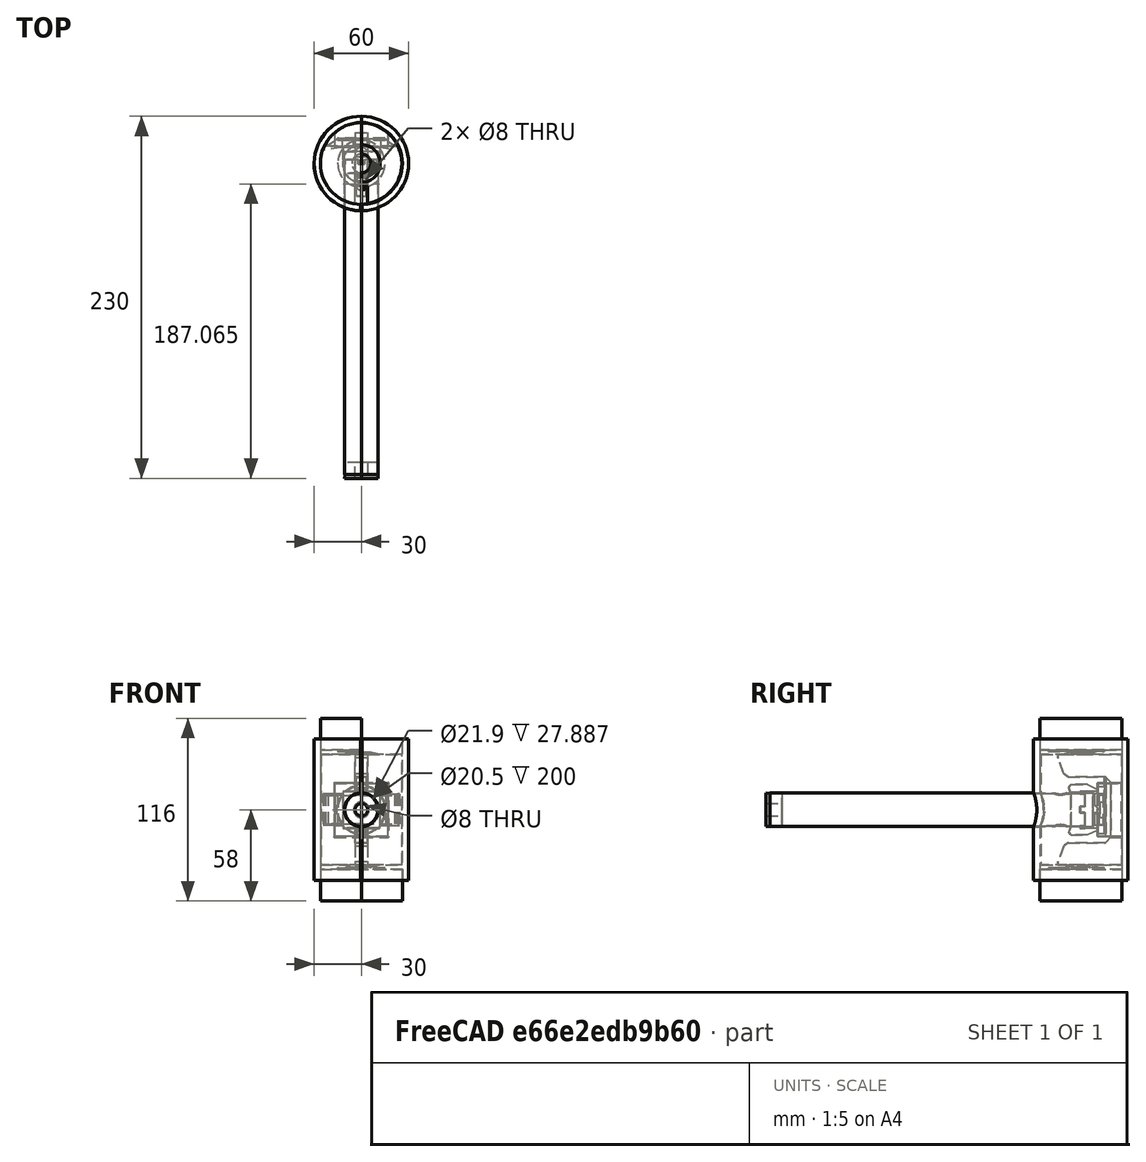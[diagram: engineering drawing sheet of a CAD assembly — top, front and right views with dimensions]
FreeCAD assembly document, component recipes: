
FREECAD ASSEMBLY — COMPONENT RECIPES ("HammerWithDrawings")

This assembly document has 13 components, labeled P0..P12 below (a component is one placed body or linked part). 13 of them carry a construction recipe — the FreeCAD feature program that regenerates the part from scratch, quoted from this document or its linked companion documents; the rest are supplied as boundary geometry only. No exploded tour is included for this assembly.
COMPONENT P0 — recipe-attached ("Body001_CutLink", modeled in this document).
Construction recipe (the document's own serialized feature program — sketch geometry with constraints, then the solid features built on it; lengths are millimeters unless a unit is written):

FEATURE [Sketcher::SketchObject] Sketch005  label="top_sens_base"
  FullyConstrained = true
  MapMode = 5
  Support = -> [XY_Plane]
  expr: Constraints[18] = <<Properties>>.Clearance
  expr: Constraints[1] = <<Properties>>.Head_ID
  expr: Constraints[3] = 34 - <<Properties>>.Clearance * 2
  expr: Constraints[6] = 10.5 + <<Properties>>.Clearance
  sketch-geometry (8):
    g0: Circle CenterX=0 CenterY=0 CenterZ=0 NormalX=0 NormalY=0 NormalZ=1 AngleXU=0 Radius=25.7
    g1: LineSegment StartX=-16.8 StartY=10.7 StartZ=0 EndX=16.8 EndY=10.7 EndZ=0
    g2: GeomPoint X=0 Y=10.7 Z=0
    g3: LineSegment StartX=-16.8 StartY=10.7 StartZ=0 EndX=-16.8 EndY=19.1836 EndZ=0
    g4: LineSegment StartX=16.8 StartY=10.7 StartZ=0 EndX=16.8 EndY=19.1836 EndZ=0
    g5: GeomPoint X=0 Y=25.7 Z=0
    g6: ArcOfCircle CenterX=0 CenterY=0 CenterZ=0 NormalX=0 NormalY=0 NormalZ=1 AngleXU=0 Radius=25.5 StartAngle=0.851542 EndAngle=2.29005
    g7: GeomPoint X=0 Y=25.5 Z=0
  constraints (19):
    c: Coincident(g0,g-1)
    c: Diameter(g0) = 51.4
    c: Horizontal(g1)
    c: DistanceX(g1,g1) = 33.6
    c: Symmetric(g1,g1,g2)
    c: PointOnObject(g2,g-2)
    c: DistanceY(g0,g2) = 10.7
    c: Coincident(g3,g1)
    c: Vertical(g3)
    c: Vertical(g4)
    c: Coincident(g4,g1)
    c: PointOnObject(g5,g0)
    c: PointOnObject(g5,g-2)
    c: Coincident(g6,g0)
    c: Coincident(g6,g3)
    c: Coincident(g6,g4)
    c: PointOnObject(g7,g6)
    c: PointOnObject(g7,g-2)
    c: DistanceY(g7,g5) = 0.2
FEATURE [PartDesign::Pad] Pad001  label="Top_Base"
  Direction = (0,0,1)
  Length = 16.8
  Length2 = 16.8
  Profile = -> Sketch005
  ReferenceAxis = -> Sketch005 [N_Axis]
  Type = 4
  expr: Length = <<Properties>>.Sensor_Diameter / 2 + 2 - <<Properties>>.Clearance
  expr: Length2 = <<Properties>>.Sensor_Diameter / 2 + 2 - <<Properties>>.Clearance
FEATURE [Sketcher::SketchObject] Sketch006
  FullyConstrained = true
  MapMode = 5
  Support = -> [XY_Plane]
  expr: Constraints[1] = Sketch003.Constraints[1]
  expr: Constraints[22] = Sketch003.Constraints[22]
  expr: Constraints[23] = Sketch003.Constraints[23]
  expr: Constraints[33] = Sketch003.Constraints[33]
  expr: Constraints[35] = Sketch003.Constraints[35]
  expr: Constraints[38] = Sketch003.Constraints[38]
  expr: Constraints[3] = Sketch003.Constraints[3]
  expr: Constraints[7] = Sketch003.Constraints[7]
  sketch-geometry (15):
    g0: Circle CenterX=0 CenterY=0 CenterZ=0 NormalX=0 NormalY=0 NormalZ=1 AngleXU=0 Radius=25.7
    g1: LineSegment StartX=-15.2 StartY=15.4669 StartZ=0 EndX=15.2 EndY=15.4669 EndZ=0
    g2: GeomPoint X=0 Y=15.4669 Z=0
    g3: LineSegment StartX=-23 StartY=11.4669 StartZ=0 EndX=23 EndY=11.4669 EndZ=0
    g4: GeomPoint X=0 Y=11.4669 Z=0
    g5: LineSegment StartX=-15.2 StartY=15.4669 StartZ=0 EndX=-21 EndY=11.4669 EndZ=0
    g6: LineSegment StartX=15.2 StartY=15.4669 StartZ=0 EndX=21 EndY=11.4669 EndZ=0
    g7: LineSegment StartX=21 StartY=11.4669 StartZ=0 EndX=23 EndY=11.4669 EndZ=0
    g8: LineSegment StartX=-21 StartY=11.4669 StartZ=0 EndX=-23 EndY=11.4669 EndZ=0
    g9: ArcOfCircle CenterX=0 CenterY=0 CenterZ=0 NormalX=0 NormalY=0 NormalZ=1 AngleXU=0 Radius=25.7 StartAngle=2.6791 EndAngle=2.80587
    g10: ArcOfCircle CenterX=0 CenterY=0 CenterZ=0 NormalX=0 NormalY=0 NormalZ=1 AngleXU=0 Radius=25.7 StartAngle=0.335723 EndAngle=0.462496
    g11: LineSegment StartX=-11 StartY=10.5 StartZ=0 EndX=-24.2652 EndY=8.46691 EndZ=0
    g12: LineSegment StartX=11 StartY=10.5 StartZ=0 EndX=24.2652 EndY=8.46691 EndZ=0
    g13: LineSegment StartX=11 StartY=10.5 StartZ=0 EndX=-11 EndY=10.5 EndZ=0
    g14: GeomPoint X=0 Y=10.5 Z=0
  constraints (40):
    c: Coincident(g0,g-1)
    c: Diameter(g0) = 51.4
    c: Horizontal(g1)
    c: DistanceX(g1,g1) = 30.4
    c: Symmetric(g1,g1,g2)
    c: PointOnObject(g2,g-2)
    c: Horizontal(g3)
    c: DistanceX(g3,g3) = 46
    c: Symmetric(g3,g3,g4)
    c: PointOnObject(g4,g-2)
    c: Coincident(g5,g1)
    c: PointOnObject(g5,g3)
    c: Coincident(g6,g1)
    c: PointOnObject(g6,g3)
    c: Coincident(g7,g6)
    c: PointOnObject(g7,g0)
    c: Horizontal(g7)
    c: Coincident(g8,g5)
    c: PointOnObject(g8,g0)
    c: Horizontal(g8)
    c: Equal(g8,g7)
    c: PointOnObject(g3,g0)
    c: DistanceY(g6,g1) = 4
    c: DistanceX(g6,g7) = 2
    c: Coincident(g9,g0)
    c: Coincident(g9,g8)
    c: Coincident(g10,g9)
    c: Coincident(g10,g7)
    c: Coincident(g13,g12)
    c: Coincident(g13,g11)
    c: Horizontal(g13)
    c: Coincident(g10,g12)
    c: Coincident(g9,g11)
    c: DistanceX(g12,g6) = 10
    c: Equal(g12,g11)
    c: DistanceY(g10,g7) = 3
    c: Symmetric(g13,g13,g14)
    c: PointOnObject(g14,g-2)
    c: DistanceY(g9,g14) = 10.5
    c: DistanceY(g9,g2) = 15.4669
FEATURE [PartDesign::Pocket] Pocket004
  BaseFeature = -> Pad001
  Direction = (0,0,-1)
  Length = 9.5
  Length2 = 9.5
  Profile = -> Sketch006
  ReferenceAxis = -> Sketch006 [N_Axis]
  Type = 4
FEATURE [PartDesign::Chamfer] Chamfer002
  Angle = 45
  Base = -> Pocket004 [Edge22,Edge12]
  BaseFeature = -> Pocket004
  ChamferType = 0
  FlipDirection = false
  Size = 0.3
  Size2 = 1
  SupportTransform = false
  UseAllEdges = false
FEATURE [Sketcher::SketchObject] Sketch007
  FullyConstrained = true
  MapMode = 5
  Placement = pos=(0,0,0) rot=(1,0,0;1.5708rad)
  Support = -> [XZ_Plane]
  expr: Constraints[11] = <<Properties>>.Sensor_Wire_Track_Width
  expr: Constraints[1] = <<Properties>>.Sensor_Diameter + 1
  expr: Constraints[27] = <<Properties>>.Sensor_Wire_Track_Width
  sketch-geometry (11):
    g0: Circle CenterX=0 CenterY=0 CenterZ=0 NormalX=0 NormalY=0 NormalZ=1 AngleXU=0 Radius=15.5
    g1: LineSegment StartX=-4 StartY=14.975 StartZ=0 EndX=-4 EndY=27.305 EndZ=0
    g2: LineSegment StartX=-4 StartY=27.305 StartZ=0 EndX=4 EndY=27.305 EndZ=0
    g3: LineSegment StartX=4 StartY=27.305 StartZ=0 EndX=4 EndY=14.975 EndZ=0
    g4: GeomPoint X=0 Y=27.305 Z=0
    g5: LineSegment StartX=-4 StartY=-14.975 StartZ=0 EndX=-4 EndY=-27.305 EndZ=0
    g6: LineSegment StartX=-4 StartY=-27.305 StartZ=0 EndX=4 EndY=-27.305 EndZ=0
    g7: LineSegment StartX=4 StartY=-27.305 StartZ=0 EndX=4 EndY=-14.975 EndZ=0
    g8: GeomPoint X=0 Y=-27.305 Z=0
    g9: ArcOfCircle CenterX=0 CenterY=0 CenterZ=0 NormalX=0 NormalY=0 NormalZ=1 AngleXU=0 Radius=15.5 StartAngle=1.83181 EndAngle=4.45137
    g10: ArcOfCircle CenterX=0 CenterY=0 CenterZ=0 NormalX=0 NormalY=0 NormalZ=1 AngleXU=0 Radius=15.5 StartAngle=4.97341 EndAngle=7.59296
  constraints (28):
    c: Coincident(g0,g-1)
    c: Diameter(g0) = 31
    c: PointOnObject(g1,g0)
    c: Vertical(g1)
    c: Coincident(g2,g1)
    c: Horizontal(g2)
    c: Coincident(g3,g2)
    c: PointOnObject(g3,g0)
    c: Vertical(g3)
    c: Symmetric(g2,g2,g4)
    c: PointOnObject(g4,g-2)
    c: DistanceX(g2,g2) = 8
    c: DistanceY(g3,g3) = 12.33
    c: Vertical(g5)
    c: Coincident(g6,g5)
    c: Horizontal(g6)
    c: Coincident(g7,g6)
    c: Vertical(g7)
    c: Symmetric(g6,g6,g8)
    c: PointOnObject(g8,g-2)
    c: Equal(g7,g3)
    c: Coincident(g9,g0)
    c: Coincident(g9,g1)
    c: Coincident(g9,g5)
    c: Coincident(g10,g9)
    c: Coincident(g10,g3)
    c: Coincident(g10,g7)
    c: DistanceX(g6,g6) = 8
FEATURE [PartDesign::Pocket] Pocket005
  BaseFeature = -> Chamfer002
  Direction = (0,1,2e-16)
  Length = 0
  Length2 = 5
  Offset = 0.4
  Profile = -> Sketch007
  ReferenceAxis = -> Sketch007 [N_Axis]
  Type = 3
  UpToFace = -> Chamfer002 [Face11]
FEATURE [PartDesign::Body] Body001  label="TopSensor"
  Group = -> [Sketch005,Pad001,Sketch006,Pocket004,Chamfer002,Sketch007,Pocket005]
  Origin = -> Origin
  Tip = -> Pocket005
COMPONENT P1 — recipe-attached ("Body002_CutLink", modeled in this document).
Construction recipe (the document's own serialized feature program — sketch geometry with constraints, then the solid features built on it; lengths are millimeters unless a unit is written):

FEATURE [Sketcher::SketchObject] Sketch009
  FullyConstrained = true
  MapMode = 5
  Support = -> [XY_Plane002]
  sketch-geometry (2):
    g0: Circle CenterX=0 CenterY=0 CenterZ=0 NormalX=0 NormalY=0 NormalZ=1 AngleXU=0 Radius=26
    g1: Circle CenterX=0 CenterY=0 CenterZ=0 NormalX=0 NormalY=0 NormalZ=1 AngleXU=0 Radius=30
  constraints (4):
    c: Coincident(g0,g-1)
    c: Coincident(g1,g0)
    c: Diameter(g0) = 52
    c: Diameter(g1) = 60
FEATURE [PartDesign::Pad] Pad002
  Direction = (0,0,1)
  Length = 45
  Length2 = 45
  Profile = -> Sketch009
  ReferenceAxis = -> Sketch009 [N_Axis]
  Type = 4
FEATURE [Sketcher::SketchObject] Sketch010
  FullyConstrained = true
  MapMode = 5
  Placement = pos=(0,0,0) rot=(1,0,0;1.5708rad)
  Support = -> [XZ_Plane002]
  expr: Constraints[1] = <<Properties>>.Handle_OD
  sketch-geometry (1):
    g0: Circle CenterX=0 CenterY=0 CenterZ=0 NormalX=0 NormalY=0 NormalZ=1 AngleXU=0 Radius=10.75
  constraints (2):
    c: Coincident(g0,g-1)
    c: Diameter(g0) = 21.5
FEATURE [PartDesign::Pocket] Pocket007
  BaseFeature = -> Pad002
  Direction = (0,1,2e-16)
  Length = 5
  Length2 = 5
  Profile = -> Sketch010
  ReferenceAxis = -> Sketch010 [N_Axis]
  Reversed = true
  Type = 1
FEATURE [Sketcher::SketchObject] Sketch027
  FullyConstrained = true
  MapMode = 5
  Placement = pos=(0,0,0) rot=(1,0,0;1.5708rad)
  Support = -> [XZ_Plane002]
  sketch-geometry (5):
    g0: LineSegment StartX=-0.5 StartY=-45 StartZ=0 EndX=-0.5 EndY=45 EndZ=0
    g1: LineSegment StartX=-0.5 StartY=45 StartZ=0 EndX=0.5 EndY=45 EndZ=0
    g2: LineSegment StartX=0.5 StartY=45 StartZ=0 EndX=0.5 EndY=-45 EndZ=0
    g3: LineSegment StartX=0.5 StartY=-45 StartZ=0 EndX=-0.5 EndY=-45 EndZ=0
    g4: GeomPoint X=0 Y=0 Z=0
  constraints (12):
    c: Coincident(g0,g1)
    c: Coincident(g1,g2)
    c: Coincident(g2,g3)
    c: Coincident(g3,g0)
    c: Horizontal(g1)
    c: Horizontal(g3)
    c: Vertical(g0)
    c: Vertical(g2)
    c: Symmetric(g1,g0,g4)
    c: Coincident(g4,g-1)
    c: DistanceX(g1,g1) = 1
    c: DistanceY(g2,g2) = 90
FEATURE [PartDesign::Pocket] Pocket012
  BaseFeature = -> Pocket007
  Direction = (0,1,2e-16)
  Length = 5
  Length2 = 5
  Profile = -> Sketch027
  ReferenceAxis = -> Sketch027 [N_Axis]
  Reversed = true
  Type = 1
FEATURE [PartDesign::Body] Body002  label="PVCHammerHeadShell"
  Group = -> [Sketch009,Pad002,Sketch010,Pocket007,Sketch027,Pocket012]
  Origin = -> Origin002
  Tip = -> Pocket012
COMPONENT P2 — recipe-attached ("Body003_CutLink", modeled in this document).
Construction recipe (the document's own serialized feature program — sketch geometry with constraints, then the solid features built on it; lengths are millimeters unless a unit is written):

FEATURE [Sketcher::SketchObject] Sketch011
  FullyConstrained = true
  MapMode = 5
  Placement = pos=(0,0,0) rot=(1,0,0;1.5708rad)
  Support = -> [XZ_Plane003]
  expr: Constraints[3] = <<Properties>>.Handle_ID
  sketch-geometry (2):
    g0: Circle CenterX=0 CenterY=0 CenterZ=0 NormalX=0 NormalY=0 NormalZ=1 AngleXU=0 Radius=10.625
    g1: Circle CenterX=0 CenterY=0 CenterZ=0 NormalX=0 NormalY=0 NormalZ=1 AngleXU=0 Radius=10.25
  constraints (4):
    c: Coincident(g0,g-1)
    c: Diameter(g0) = 21.25
    c: Coincident(g1,g0)
    c: Diameter(g1) = 20.5
FEATURE [PartDesign::Pad] Pad003
  Direction = (0,-1,-2e-16)
  Length = 200
  Length2 = 10
  Placement = pos=(0,0,0) rot=(1,0,0;1.5708rad)
  Profile = -> Sketch011
  ReferenceAxis = -> Sketch011 [N_Axis]
  Type = 0
FEATURE [Sketcher::SketchObject] Sketch018
  FullyConstrained = false
  MapMode = 5
  Support = -> [XY_Plane003]
  sketch-geometry (1):
    g0: Circle CenterX=0 CenterY=-15.4348 CenterZ=0 NormalX=0 NormalY=0 NormalZ=1 AngleXU=0 Radius=4
  constraints (2):
    c: PointOnObject(g0,g-2)
    c: Diameter(g0) = 8
FEATURE [PartDesign::Pocket] Pocket008
  BaseFeature = -> Pad003
  Direction = (0,0,-1)
  Length = 50
  Length2 = 50
  Placement = pos=(0,0,0) rot=(1,0,0;1.5708rad)
  Profile = -> Sketch018
  ReferenceAxis = -> Sketch018 [N_Axis]
  Type = 4
FEATURE [Sketcher::SketchObject] Sketch019
  FullyConstrained = true
  MapMode = 5
  Placement = pos=(0,0,0) rot=(1,0,0;1.5708rad)
  Support = -> [XZ_Plane003]
  sketch-geometry (17):
    g0: LineSegment StartX=12 StartY=-2 StartZ=0 EndX=12 EndY=2 EndZ=0
    g1: LineSegment StartX=12 StartY=2 StartZ=0 EndX=2 EndY=2 EndZ=0
    g2: LineSegment StartX=2 StartY=2 StartZ=0 EndX=2 EndY=12 EndZ=0
    g3: LineSegment StartX=2 StartY=12 StartZ=0 EndX=-2 EndY=12 EndZ=0
    g4: LineSegment StartX=-2 StartY=12 StartZ=0 EndX=-2 EndY=2 EndZ=0
    g5: LineSegment StartX=-2 StartY=2 StartZ=0 EndX=-12 EndY=2 EndZ=0
    g6: LineSegment StartX=-12 StartY=2 StartZ=0 EndX=-12 EndY=-2 EndZ=0
    g7: LineSegment StartX=-12 StartY=-2 StartZ=0 EndX=-2 EndY=-2 EndZ=0
    g8: LineSegment StartX=-2 StartY=-2 StartZ=0 EndX=-2 EndY=-12 EndZ=0
    g9: LineSegment StartX=-2 StartY=-12 StartZ=0 EndX=2 EndY=-12 EndZ=0
    g10: LineSegment StartX=2 StartY=-12 StartZ=0 EndX=2 EndY=-2 EndZ=0
    g11: LineSegment StartX=2 StartY=-2 StartZ=0 EndX=12 EndY=-2 EndZ=0
    g12: LineSegment StartX=-2 StartY=-2 StartZ=0 EndX=-2 EndY=2 EndZ=0
    g13: LineSegment StartX=-2 StartY=2 StartZ=0 EndX=2 EndY=2 EndZ=0
    g14: LineSegment StartX=2 StartY=2 StartZ=0 EndX=2 EndY=-2 EndZ=0
    g15: LineSegment StartX=2 StartY=-2 StartZ=0 EndX=-2 EndY=-2 EndZ=0
    g16: GeomPoint X=0 Y=0 Z=0
  constraints (46):
    c: Vertical(g0)
    c: Coincident(g1,g0)
    c: Horizontal(g1)
    c: Coincident(g2,g1)
    c: Vertical(g2)
    c: Coincident(g3,g2)
    c: Horizontal(g3)
    c: Coincident(g4,g3)
    c: Vertical(g4)
    c: Coincident(g5,g4)
    c: Horizontal(g5)
    c: Coincident(g6,g5)
    c: Vertical(g6)
    c: Horizontal(g7)
    c: Coincident(g8,g7)
    c: Vertical(g8)
    c: Horizontal(g9)
    c: Coincident(g10,g9)
    c: Vertical(g10)
    c: Coincident(g11,g10)
    c: Coincident(g11,g0)
    c: Horizontal(g11)
    c: Equal(g0,g3)
    c: Equal(g3,g6)
    c: Equal(g6,g9)
    c: Coincident(g6,g7)
    c: Coincident(g9,g8)
    c: Equal(g11,g7)
    c: Equal(g11,g1)
    c: Equal(g2,g4)
    c: Equal(g5,g10)
    c: Coincident(g12,g13)
    c: Coincident(g13,g14)
    c: Coincident(g14,g15)
    c: Coincident(g15,g12)
    c: Horizontal(g13)
    c: Horizontal(g15)
    c: Vertical(g12)
    c: Vertical(g14)
    c: Symmetric(g13,g12,g16)
    c: Coincident(g16,g-1)
    c: Coincident(g13,g1)
    c: Coincident(g7,g12)
    c: DistanceX(g13,g13) = 4
    c: DistanceY(g2,g2) = 10
    c: Equal(g10,g2)
FEATURE [PartDesign::Pocket] Pocket009
  BaseFeature = -> Pocket008
  Direction = (0,1,2e-16)
  Length = 3
  Length2 = 5
  Placement = pos=(0,0,0) rot=(1,0,0;1.5708rad)
  Profile = -> Sketch019
  ReferenceAxis = -> Sketch019 [N_Axis]
  Reversed = true
  Type = 0
FEATURE [PartDesign::Body] Body003  label="MetalHandle"
  Group = -> [Sketch011,Pad003,Sketch018,Pocket008,Sketch019,Pocket009]
  Origin = -> Origin003
  Placement = pos=(0,2.5,0) rot=(0,0,1;0rad)
  Tip = -> Pocket009
COMPONENT P3 — recipe-attached ("Body005_CutLink", modeled in this document).
Construction recipe (the document's own serialized feature program — sketch geometry with constraints, then the solid features built on it; lengths are millimeters unless a unit is written):

FEATURE [Sketcher::SketchObject] Sketch014
  FullyConstrained = true
  MapMode = 5
  Support = -> [XY_Plane005]
  sketch-geometry (5):
    g0: ArcOfCircle CenterX=0 CenterY=0 CenterZ=0 NormalX=0 NormalY=0 NormalZ=1 AngleXU=0 Radius=15 StartAngle=4.90695 EndAngle=10.801
    g1: LineSegment StartX=2.9 StartY=-14.717 StartZ=0 EndX=2.9 EndY=-20.717 EndZ=0
    g2: LineSegment StartX=2.9 StartY=-20.717 StartZ=0 EndX=-2.9 EndY=-20.717 EndZ=0
    g3: LineSegment StartX=-2.9 StartY=-20.717 StartZ=0 EndX=-2.9 EndY=-14.717 EndZ=0
    g4: LineSegment StartX=2.9 StartY=-14.717 StartZ=0 EndX=-2.9 EndY=-14.717 EndZ=0
  constraints (14):
    c: Coincident(g0,g-1)
    c: Radius(g0) = 15
    c: Coincident(g1,g0)
    c: Vertical(g1)
    c: Coincident(g2,g1)
    c: Horizontal(g2)
    c: Coincident(g3,g2)
    c: Coincident(g3,g0)
    c: Vertical(g3)
    c: DistanceX(g2,g2) = 5.8
    c: Coincident(g4,g0)
    c: Coincident(g4,g0)
    c: Horizontal(g4)
    c: DistanceY(g1,g1) = 6
FEATURE [PartDesign::Pad] Pad007
  Direction = (0,0,1)
  Length = 1
  Length2 = 10
  Profile = -> Sketch014
  ReferenceAxis = -> Sketch014 [N_Axis]
  Type = 0
FEATURE [PartDesign::Body] Body005  label="Sensor1"
  Group = -> [Sketch014,Pad007]
  Origin = -> Origin005
  Placement = pos=(0,0,37) rot=(0,0,1;0rad)
  Tip = -> Pad007
COMPONENT P4 — recipe-attached ("Body006_CutLink", modeled in this document).
Construction recipe (the document's own serialized feature program — sketch geometry with constraints, then the solid features built on it; lengths are millimeters unless a unit is written):

FEATURE [PartDesign::FeatureBase] Clone
  BaseFeature = -> Body005
FEATURE [PartDesign::Body] Body006  label="Sensor2"
  Group = -> [Clone]
  Origin = -> Origin006
  Placement = pos=(0,0,-37) rot=(0,1,0;3.14159rad)
  Tip = -> Clone
COMPONENT P5 — recipe-attached ("Body007_CutLink", modeled in this document).
Construction recipe (the document's own serialized feature program — sketch geometry with constraints, then the solid features built on it; lengths are millimeters unless a unit is written):

FEATURE [PartDesign::FeatureBase] Clone001
  BaseFeature = -> Body005
FEATURE [PartDesign::Body] Body007  label="Sensor3"
  Group = -> [Clone001]
  Origin = -> Origin007
  Placement = pos=(0,16,-4e-15) rot=(0,0.707107,-0.707107;3.14159rad)
  Tip = -> Clone001
COMPONENT P6 — recipe-attached ("Body008_CutLink", modeled in this document).
Construction recipe (the document's own serialized feature program — sketch geometry with constraints, then the solid features built on it; lengths are millimeters unless a unit is written):

FEATURE [Sketcher::SketchObject] Sketch015
  FullyConstrained = true
  MapMode = 5
  Support = -> [XY_Plane008]
  sketch-geometry (1):
    g0: Circle CenterX=0 CenterY=0 CenterZ=0 NormalX=0 NormalY=0 NormalZ=1 AngleXU=0 Radius=26
  constraints (2):
    c: Coincident(g0,g-1)
    c: Diameter(g0) = 52
FEATURE [PartDesign::Pad] Pad008
  Direction = (0,0,1)
  Length = 20
  Length2 = 10
  Profile = -> Sketch015
  ReferenceAxis = -> Sketch015 [N_Axis]
  Type = 0
FEATURE [PartDesign::Body] Body008  label="Foam1"
  Group = -> [Sketch015,Pad008]
  Origin = -> Origin008
  Placement = pos=(0,0,38) rot=(0,0,1;0rad)
  Tip = -> Pad008
COMPONENT P7 — recipe-attached ("Body009_CutLink", modeled in this document).
Construction recipe (the document's own serialized feature program — sketch geometry with constraints, then the solid features built on it; lengths are millimeters unless a unit is written):

FEATURE [PartDesign::FeatureBase] Clone002
  BaseFeature = -> Body008
  Placement = pos=(0,0,38) rot=(0,0,1;0rad)
FEATURE [PartDesign::Body] Body009  label="Foam2"
  Group = -> [Clone002]
  Origin = -> Origin009
  Placement = pos=(0,0,0) rot=(1,0,0;3.14159rad)
  Tip = -> Clone002
COMPONENT P8 — recipe-attached ("Body010_CutLink", modeled in this document).
Construction recipe (the document's own serialized feature program — sketch geometry with constraints, then the solid features built on it; lengths are millimeters unless a unit is written):

FEATURE [Sketcher::SketchObject] Sketch016
  FullyConstrained = true
  MapMode = 5
  Support = -> [XY_Plane010]
  sketch-geometry (5):
    g0: LineSegment StartX=-22.5 StartY=-0.4 StartZ=0 EndX=-22.5 EndY=0.4 EndZ=0
    g1: LineSegment StartX=-22.5 StartY=0.4 StartZ=0 EndX=22.5 EndY=0.4 EndZ=0
    g2: LineSegment StartX=22.5 StartY=0.4 StartZ=0 EndX=22.5 EndY=-0.4 EndZ=0
    g3: LineSegment StartX=22.5 StartY=-0.4 StartZ=0 EndX=-22.5 EndY=-0.4 EndZ=0
    g4: GeomPoint X=0 Y=0 Z=0
  constraints (12):
    c: Coincident(g0,g1)
    c: Coincident(g1,g2)
    c: Coincident(g2,g3)
    c: Coincident(g3,g0)
    c: Horizontal(g1)
    c: Horizontal(g3)
    c: Vertical(g0)
    c: Vertical(g2)
    c: Symmetric(g1,g0,g4)
    c: Coincident(g4,g-1)
    c: DistanceX(g1,g1) = 45
    c: DistanceY(g2,g2) = 0.8
FEATURE [PartDesign::Pad] Pad009
  Direction = (0,0,1)
  Length = 9
  Length2 = 9
  Profile = -> Sketch016
  ReferenceAxis = -> Sketch016 [N_Axis]
  Type = 4
FEATURE [PartDesign::Body] Body010  label="ShimStock"
  Group = -> [Sketch016,Pad009]
  Origin = -> Origin010
  Placement = pos=(0,11,0) rot=(0,0,1;0rad)
  Tip = -> Pad009
COMPONENT P9 — recipe-attached ("Body011_CutLink", modeled in this document).
Construction recipe (the document's own serialized feature program — sketch geometry with constraints, then the solid features built on it; lengths are millimeters unless a unit is written):

FEATURE [Sketcher::SketchObject] Sketch017
  FullyConstrained = true
  MapMode = 5
  Placement = pos=(0,0,0) rot=(1,0,0;1.5708rad)
  Support = -> [XZ_Plane011]
  sketch-geometry (1):
    g0: Circle CenterX=0 CenterY=0 CenterZ=0 NormalX=0 NormalY=0 NormalZ=1 AngleXU=0 Radius=5
  constraints (2):
    c: Coincident(g0,g-1)
    c: Diameter(g0) = 10
FEATURE [PartDesign::Pad] Pad010
  Direction = (0,-1,-2e-16)
  Length = 3
  Length2 = 10
  Placement = pos=(0,0,0) rot=(1,0,0;1.5708rad)
  Profile = -> Sketch017
  ReferenceAxis = -> Sketch017 [N_Axis]
  Type = 0
FEATURE [PartDesign::Body] Body011  label="TopFoam"
  Group = -> [Sketch017,Pad010]
  Origin = -> Origin011
  Placement = pos=(0,15,0) rot=(0,0,1;0rad)
  Tip = -> Pad010
COMPONENT P10 — recipe-attached ("Body012_CutLink", modeled in this document).
Construction recipe (the document's own serialized feature program — sketch geometry with constraints, then the solid features built on it; lengths are millimeters unless a unit is written):

FEATURE [Sketcher::SketchObject] Sketch020
  FullyConstrained = true
  MapMode = 5
  Placement = pos=(0,0,0) rot=(1,0,0;1.5708rad)
  Support = -> [XZ_Plane012]
  expr: Constraints[43] = Sketch019.Constraints[43]
  expr: Constraints[44] = Sketch019.Constraints[44]
  expr: Constraints[77] = <<Properties>>.Clearance
  expr: Constraints[78] = <<Properties>>.Clearance
  expr: Constraints[79] = <<Properties>>.Clearance
  expr: Constraints[81] = (<<Properties>>.Handle_OD + 2) / 2 - <<Properties>>.Clearance
  sketch-geometry (29):
    g0: LineSegment StartX=12 StartY=-2 StartZ=0 EndX=12 EndY=2 EndZ=0
    g1: LineSegment StartX=12 StartY=2 StartZ=0 EndX=2 EndY=2 EndZ=0
    g2: LineSegment StartX=2 StartY=2 StartZ=0 EndX=2 EndY=12 EndZ=0
    g3: LineSegment StartX=2 StartY=12 StartZ=0 EndX=-2 EndY=12 EndZ=0
    g4: LineSegment StartX=-2 StartY=12 StartZ=0 EndX=-2 EndY=2 EndZ=0
    g5: LineSegment StartX=-2 StartY=2 StartZ=0 EndX=-12 EndY=2 EndZ=0
    g6: LineSegment StartX=-12 StartY=2 StartZ=0 EndX=-12 EndY=-2 EndZ=0
    g7: LineSegment StartX=-12 StartY=-2 StartZ=0 EndX=-2 EndY=-2 EndZ=0
    g8: LineSegment StartX=-2 StartY=-2 StartZ=0 EndX=-2 EndY=-12 EndZ=0
    g9: LineSegment StartX=-2 StartY=-12 StartZ=0 EndX=2 EndY=-12 EndZ=0
    g10: LineSegment StartX=2 StartY=-12 StartZ=0 EndX=2 EndY=-2 EndZ=0
    g11: LineSegment StartX=2 StartY=-2 StartZ=0 EndX=12 EndY=-2 EndZ=0
    g12: LineSegment StartX=-2 StartY=-2 StartZ=0 EndX=-2 EndY=2 EndZ=0
    g13: LineSegment StartX=-2 StartY=2 StartZ=0 EndX=2 EndY=2 EndZ=0
    g14: LineSegment StartX=2 StartY=2 StartZ=0 EndX=2 EndY=-2 EndZ=0
    g15: LineSegment StartX=2 StartY=-2 StartZ=0 EndX=-2 EndY=-2 EndZ=0
    g16: GeomPoint X=0 Y=0 Z=0
    g17: LineSegment StartX=-1.8 StartY=11.55 StartZ=0 EndX=-1.8 EndY=1.8 EndZ=0
    g18: LineSegment StartX=-1.8 StartY=1.8 StartZ=0 EndX=-11.55 EndY=1.8 EndZ=0
    g19: LineSegment StartX=-11.55 StartY=1.8 StartZ=0 EndX=-11.55 EndY=-1.8 EndZ=0
    g20: LineSegment StartX=-11.55 StartY=-1.8 StartZ=0 EndX=-1.8 EndY=-1.8 EndZ=0
    g21: LineSegment StartX=-1.8 StartY=-1.8 StartZ=0 EndX=-1.8 EndY=-11.55 EndZ=0
    g22: LineSegment StartX=-1.8 StartY=-11.55 StartZ=0 EndX=1.8 EndY=-11.55 EndZ=0
    g23: LineSegment StartX=1.8 StartY=-11.55 StartZ=0 EndX=1.8 EndY=-1.8 EndZ=0
    g24: LineSegment StartX=1.8 StartY=-1.8 StartZ=0 EndX=11.55 EndY=-1.8 EndZ=0
    g25: LineSegment StartX=11.55 StartY=-1.8 StartZ=0 EndX=11.55 EndY=1.8 EndZ=0
    g26: LineSegment StartX=11.55 StartY=1.8 StartZ=0 EndX=1.8 EndY=1.8 EndZ=0
    g27: LineSegment StartX=1.8 StartY=1.8 StartZ=0 EndX=1.8 EndY=11.55 EndZ=0
    g28: LineSegment StartX=1.8 StartY=11.55 StartZ=0 EndX=-1.8 EndY=11.55 EndZ=0
  constraints (82):
    c: Vertical(g0)
    c: Coincident(g1,g0)
    c: Horizontal(g1)
    c: Coincident(g2,g1)
    c: Vertical(g2)
    c: Coincident(g3,g2)
    c: Horizontal(g3)
    c: Coincident(g4,g3)
    c: Vertical(g4)
    c: Coincident(g5,g4)
    c: Horizontal(g5)
    c: Coincident(g6,g5)
    c: Vertical(g6)
    c: Horizontal(g7)
    c: Coincident(g8,g7)
    c: Vertical(g8)
    c: Horizontal(g9)
    c: Coincident(g10,g9)
    c: Vertical(g10)
    c: Coincident(g11,g10)
    c: Coincident(g11,g0)
    c: Horizontal(g11)
    c: Equal(g0,g3)
    c: Equal(g3,g6)
    c: Equal(g6,g9)
    c: Coincident(g6,g7)
    c: Coincident(g9,g8)
    c: Equal(g11,g7)
    c: Equal(g11,g1)
    c: Equal(g2,g4)
    c: Equal(g5,g10)
    c: Coincident(g12,g13)
    c: Coincident(g13,g14)
    c: Coincident(g14,g15)
    c: Coincident(g15,g12)
    c: Horizontal(g13)
    c: Horizontal(g15)
    c: Vertical(g12)
    c: Vertical(g14)
    c: Symmetric(g13,g12,g16)
    c: Coincident(g16,g-1)
    c: Coincident(g13,g1)
    c: Coincident(g7,g12)
    c: DistanceX(g13,g13) = 4
    c: DistanceY(g2,g2) = 10
    c: Equal(g10,g2)
    c: Vertical(g17)
    c: Coincident(g18,g17)
    c: Horizontal(g18)
    c: Coincident(g19,g18)
    c: Vertical(g19)
    c: Coincident(g20,g19)
    c: Horizontal(g20)
    c: Coincident(g21,g20)
    c: Vertical(g21)
    c: Coincident(g22,g21)
    c: Horizontal(g22)
    c: Coincident(g23,g22)
    c: Vertical(g23)
    c: Coincident(g24,g23)
    c: Horizontal(g24)
    c: Coincident(g25,g24)
    c: Vertical(g25)
    c: Coincident(g26,g25)
    c: Horizontal(g26)
    c: Coincident(g27,g26)
    c: Vertical(g27)
    c: Coincident(g28,g27)
    c: Coincident(g28,g17)
    c: Horizontal(g28)
    c: Equal(g26,g18)
    c: Equal(g27,g17)
    c: Equal(g26,g24)
    c: Equal(g20,g24)
    c: Equal(g21,g23)
    c: Equal(g23,g27)
    c: Equal(g22,g25)
    c: DistanceX(g26,g1) = 0.2
    c: DistanceY(g26,g1) = 0.2
    c: DistanceY(g0,g24) = 0.2
    c: Equal(g23,g24)
    c: DistanceX(g16,g25) = 11.55
FEATURE [PartDesign::Pad] Pad011
  Direction = (0,-1,2e-16)
  Length = 2.8
  Length2 = 10
  Placement = pos=(0,0,0) rot=(1,0,0;1.5708rad)
  Profile = -> Sketch020
  ReferenceAxis = -> Sketch020 [N_Axis]
  Type = 0
FEATURE [Sketcher::SketchObject] Sketch021
  FullyConstrained = true
  MapMode = 5
  Placement = pos=(0,0,0) rot=(1,0,0;1.5708rad)
  Support = -> [XZ_Plane012]
  expr: Constraints[53] = Sketch020.Constraints[43]
  expr: Constraints[54] = Sketch020.Constraints[44]
  expr: Constraints[87] = Sketch020.Constraints[77]
  expr: Constraints[88] = Sketch020.Constraints[78]
  expr: Constraints[89] = Sketch020.Constraints[79]
  expr: Constraints[91] = Sketch020.Constraints[81]
  sketch-geometry (34):
    g0: LineSegment StartX=11.55 StartY=11.55 StartZ=0 EndX=11.55 EndY=-11.55 EndZ=0
    g1: LineSegment StartX=11.55 StartY=-11.55 StartZ=0 EndX=-11.55 EndY=-11.55 EndZ=0
    g2: LineSegment StartX=-11.55 StartY=-11.55 StartZ=0 EndX=-11.55 EndY=11.55 EndZ=0
    g3: LineSegment StartX=-11.55 StartY=11.55 StartZ=0 EndX=11.55 EndY=11.55 EndZ=0
    g4: GeomPoint X=0 Y=0 Z=0
    g5: LineSegment StartX=12 StartY=-2 StartZ=0 EndX=12 EndY=2 EndZ=0
    g6: LineSegment StartX=12 StartY=2 StartZ=0 EndX=2 EndY=2 EndZ=0
    g7: LineSegment StartX=2 StartY=2 StartZ=0 EndX=2 EndY=12 EndZ=0
    g8: LineSegment StartX=2 StartY=12 StartZ=0 EndX=-2 EndY=12 EndZ=0
    g9: LineSegment StartX=-2 StartY=12 StartZ=0 EndX=-2 EndY=2 EndZ=0
    g10: LineSegment StartX=-2 StartY=2 StartZ=0 EndX=-12 EndY=2 EndZ=0
    g11: LineSegment StartX=-12 StartY=2 StartZ=0 EndX=-12 EndY=-2 EndZ=0
    g12: LineSegment StartX=-12 StartY=-2 StartZ=0 EndX=-2 EndY=-2 EndZ=0
    g13: LineSegment StartX=-2 StartY=-2 StartZ=0 EndX=-2 EndY=-12 EndZ=0
    g14: LineSegment StartX=-2 StartY=-12 StartZ=0 EndX=2 EndY=-12 EndZ=0
    g15: LineSegment StartX=2 StartY=-12 StartZ=0 EndX=2 EndY=-2 EndZ=0
    g16: LineSegment StartX=2 StartY=-2 StartZ=0 EndX=12 EndY=-2 EndZ=0
    g17: LineSegment StartX=-2 StartY=-2 StartZ=0 EndX=-2 EndY=2 EndZ=0
    g18: LineSegment StartX=-2 StartY=2 StartZ=0 EndX=2 EndY=2 EndZ=0
    g19: LineSegment StartX=2 StartY=2 StartZ=0 EndX=2 EndY=-2 EndZ=0
    g20: LineSegment StartX=2 StartY=-2 StartZ=0 EndX=-2 EndY=-2 EndZ=0
    g21: GeomPoint X=0 Y=0 Z=0
    g22: LineSegment StartX=-1.8 StartY=11.55 StartZ=0 EndX=-1.8 EndY=1.8 EndZ=0
    g23: LineSegment StartX=-1.8 StartY=1.8 StartZ=0 EndX=-11.55 EndY=1.8 EndZ=0
    g24: LineSegment StartX=-11.55 StartY=1.8 StartZ=0 EndX=-11.55 EndY=-1.8 EndZ=0
    g25: LineSegment StartX=-11.55 StartY=-1.8 StartZ=0 EndX=-1.8 EndY=-1.8 EndZ=0
    g26: LineSegment StartX=-1.8 StartY=-1.8 StartZ=0 EndX=-1.8 EndY=-11.55 EndZ=0
    g27: LineSegment StartX=-1.8 StartY=-11.55 StartZ=0 EndX=1.8 EndY=-11.55 EndZ=0
    g28: LineSegment StartX=1.8 StartY=-11.55 StartZ=0 EndX=1.8 EndY=-1.8 EndZ=0
    g29: LineSegment StartX=1.8 StartY=-1.8 StartZ=0 EndX=11.55 EndY=-1.8 EndZ=0
    g30: LineSegment StartX=11.55 StartY=-1.8 StartZ=0 EndX=11.55 EndY=1.8 EndZ=0
    g31: LineSegment StartX=11.55 StartY=1.8 StartZ=0 EndX=1.8 EndY=1.8 EndZ=0
    g32: LineSegment StartX=1.8 StartY=1.8 StartZ=0 EndX=1.8 EndY=11.55 EndZ=0
    g33: LineSegment StartX=1.8 StartY=11.55 StartZ=0 EndX=-1.8 EndY=11.55 EndZ=0
  constraints (94):
    c: Coincident(g0,g1)
    c: Coincident(g1,g2)
    c: Coincident(g2,g3)
    c: Coincident(g3,g0)
    c: Horizontal(g1)
    c: Horizontal(g3)
    c: Vertical(g0)
    c: Vertical(g2)
    c: Symmetric(g1,g0,g4)
    c: Coincident(g4,g-1)
    c: Vertical(g5)
    c: Coincident(g6,g5)
    c: Horizontal(g6)
    c: Coincident(g7,g6)
    c: Vertical(g7)
    c: Coincident(g8,g7)
    c: Horizontal(g8)
    c: Coincident(g9,g8)
    c: Vertical(g9)
    c: Coincident(g10,g9)
    c: Horizontal(g10)
    c: Coincident(g11,g10)
    c: Vertical(g11)
    c: Horizontal(g12)
    c: Coincident(g13,g12)
    c: Vertical(g13)
    c: Horizontal(g14)
    c: Coincident(g15,g14)
    c: Vertical(g15)
    c: Coincident(g16,g15)
    c: Coincident(g16,g5)
    c: Horizontal(g16)
    c: Equal(g5,g8)
    c: Equal(g8,g11)
    c: Equal(g11,g14)
    c: Coincident(g11,g12)
    c: Coincident(g14,g13)
    c: Equal(g16,g12)
    c: Equal(g16,g6)
    c: Equal(g7,g9)
    c: Equal(g10,g15)
    c: Coincident(g17,g18)
    c: Coincident(g18,g19)
    c: Coincident(g19,g20)
    c: Coincident(g20,g17)
    c: Horizontal(g18)
    c: Horizontal(g20)
    c: Vertical(g17)
    c: Vertical(g19)
    c: Symmetric(g18,g17,g21)
    c: Coincident(g21,g-1)
    c: Coincident(g18,g6)
    c: Coincident(g12,g17)
    c: DistanceX(g18,g18) = 4
    c: DistanceY(g7,g7) = 10
    c: Equal(g15,g7)
    c: Vertical(g22)
    c: Coincident(g23,g22)
    c: Horizontal(g23)
    c: Coincident(g24,g23)
    c: Vertical(g24)
    c: Coincident(g25,g24)
    c: Horizontal(g25)
    c: Coincident(g26,g25)
    c: Vertical(g26)
    c: Coincident(g27,g26)
    c: Horizontal(g27)
    c: Coincident(g28,g27)
    c: Vertical(g28)
    c: Coincident(g29,g28)
    c: Horizontal(g29)
    c: Coincident(g30,g29)
    c: Vertical(g30)
    c: Coincident(g31,g30)
    c: Horizontal(g31)
    c: Coincident(g32,g31)
    c: Vertical(g32)
    c: Coincident(g33,g32)
    c: Coincident(g33,g22)
    c: Horizontal(g33)
    c: Equal(g31,g23)
    c: Equal(g32,g22)
    c: Equal(g31,g29)
    c: Equal(g25,g29)
    c: Equal(g26,g28)
    c: Equal(g28,g32)
    c: Equal(g27,g30)
    c: DistanceX(g31,g6) = 0.2
    c: DistanceY(g31,g6) = 0.2
    c: DistanceY(g5,g29) = 0.2
    c: Equal(g28,g29)
    c: DistanceX(g21,g30) = 11.55
    c: PointOnObject(g22,g3)
    c: PointOnObject(g23,g2)
FEATURE [PartDesign::Pad] Pad012
  BaseFeature = -> Pad011
  Direction = (0,-1,2e-16)
  Length = 5
  Length2 = 10
  Placement = pos=(0,0,0) rot=(1,0,0;1.5708rad)
  Profile = -> Sketch021
  ReferenceAxis = -> Sketch021 [N_Axis]
  Reversed = true
  Type = 0
FEATURE [Sketcher::SketchObject] Sketch023
  FullyConstrained = true
  MapMode = 5
  Placement = pos=(0,5,-2.2e-15) rot=(-1,0,0;1.5708rad)
  Support = -> [Pad012]
  sketch-geometry (1):
    g0: Circle CenterX=0 CenterY=0 CenterZ=0 NormalX=0 NormalY=0 NormalZ=1 AngleXU=0 Radius=2.5
  constraints (2):
    c: Coincident(g0,g-1)
    c: Diameter(g0) = 5
FEATURE [PartDesign::Pad] Pad013
  BaseFeature = -> Pad012
  Direction = (0,1,-2e-16)
  Length = 3
  Length2 = 10
  Placement = pos=(0,0,0) rot=(1,0,0;1.5708rad)
  Profile = -> Sketch023
  ReferenceAxis = -> Sketch023 [N_Axis]
  Type = 0
FEATURE [PartDesign::Fillet] Fillet
  Base = -> Pad013 [Edge51]
  BaseFeature = -> Pad013
  Placement = pos=(0,0,0) rot=(1,0,0;1.5708rad)
  Radius = 2
  SupportTransform = false
  UseAllEdges = false
FEATURE [PartDesign::Fillet] Fillet001
  Base = -> Fillet [Edge3]
  BaseFeature = -> Fillet
  Placement = pos=(0,0,0) rot=(1,0,0;1.5708rad)
  Radius = 7
  SupportTransform = false
  UseAllEdges = false
FEATURE [Sketcher::SketchObject] Sketch025
  FullyConstrained = true
  MapMode = 5
  Placement = pos=(0,0,0) rot=(1,0,0;1.5708rad)
  Support = -> [XZ_Plane012]
  expr: Constraints[1] = <<Properties>>.Handle_OD - <<Properties>>.Clearance * 2
  sketch-geometry (1):
    g0: Circle CenterX=0 CenterY=0 CenterZ=0 NormalX=0 NormalY=0 NormalZ=1 AngleXU=0 Radius=10.55
  constraints (2):
    c: Coincident(g0,g-1)
    c: Diameter(g0) = 21.1
FEATURE [PartDesign::Pad] Pad014
  BaseFeature = -> Fillet001
  Direction = (0,-1,2e-16)
  Length = 9
  Length2 = 10
  Placement = pos=(0,0,0) rot=(1,0,0;1.5708rad)
  Profile = -> Sketch025
  ReferenceAxis = -> Sketch025 [N_Axis]
  TaperAngle = -2
  Type = 0
FEATURE [PartDesign::Chamfer] Chamfer006
  Angle = 45
  Base = -> Pad014 [Edge15,Edge19,Edge10,Edge11]
  BaseFeature = -> Pad014
  ChamferType = 0
  FlipDirection = false
  Placement = pos=(0,0,0) rot=(1,0,0;1.5708rad)
  Size = 1
  Size2 = 1
  SupportTransform = false
  UseAllEdges = false
FEATURE [PartDesign::Body] Body012  label="Pusher"
  Group = -> [Sketch020,Pad011,Sketch021,Pad012,Sketch023,Pad013,Fillet,Fillet001,Sketch025,Pad014,Chamfer006]
  Origin = -> Origin012
  Placement = pos=(0,2.5,0) rot=(0,0,1;0rad)
  Tip = -> Chamfer006
COMPONENT P11 — recipe-attached ("Body013_CutLink", modeled in this document).
Construction recipe (the document's own serialized feature program — sketch geometry with constraints, then the solid features built on it; lengths are millimeters unless a unit is written):

FEATURE [Sketcher::SketchObject] Sketch026
  FullyConstrained = true
  MapMode = 5
  Placement = pos=(0,0,0) rot=(1,0,0;1.5708rad)
  Support = -> [XZ_Plane013]
  expr: Constraints[1] = <<Properties>>.Handle_OD - 1
  sketch-geometry (2):
    g0: Circle CenterX=0 CenterY=0 CenterZ=0 NormalX=0 NormalY=0 NormalZ=1 AngleXU=0 Radius=10.25
    g1: Circle CenterX=0 CenterY=0 CenterZ=0 NormalX=0 NormalY=0 NormalZ=1 AngleXU=0 Radius=4
  constraints (4):
    c: Coincident(g0,g-1)
    c: Diameter(g0) = 20.5
    c: Coincident(g1,g0)
    c: Diameter(g1) = 8
FEATURE [PartDesign::Pad] Pad015
  Direction = (0,-1,-2e-16)
  Length = 10
  Length2 = 10
  Placement = pos=(0,0,0) rot=(1,0,0;1.5708rad)
  Profile = -> Sketch026
  ReferenceAxis = -> Sketch026 [N_Axis]
  Type = 0
FEATURE [PartDesign::Draft] Draft
  Angle = 2
  Base = -> Pad015 [Face1]
  BaseFeature = -> Pad015
  NeutralPlane = -> Pad015 [Face3]
  Placement = pos=(0,0,0) rot=(1,0,0;1.5708rad)
  SupportTransform = false
FEATURE [PartDesign::Body] Body013  label="WirePlug"
  Group = -> [Sketch026,Pad015,Draft]
  Origin = -> Origin013
  Placement = pos=(0,-190,0) rot=(0,0,1;0rad)
  Tip = -> Draft
COMPONENT P12 — recipe-attached ("Body_CutLink", modeled in this document).
Construction recipe (the document's own serialized feature program — sketch geometry with constraints, then the solid features built on it; lengths are millimeters unless a unit is written):

FEATURE [Sketcher::SketchObject] Sketch  label="base"
  FullyConstrained = true
  MapMode = 5
  Support = -> [XY_Plane001]
  expr: Constraints[1] = <<Properties>>.Head_ID
  sketch-geometry (1):
    g0: Circle CenterX=0 CenterY=0 CenterZ=0 NormalX=0 NormalY=0 NormalZ=1 AngleXU=0 Radius=25.7
  constraints (2):
    c: Coincident(g0,g-1)
    c: Diameter(g0) = 51.4
FEATURE [PartDesign::Pad] Pad  label="Base"
  Direction = (0,0,1)
  Length = 35
  Length2 = 35
  Profile = -> Sketch
  ReferenceAxis = -> Sketch [N_Axis]
  Type = 4
  expr: Length = <<Properties>>.Insert_Len / 2
  expr: Length2 = <<Properties>>.Insert_Len / 2
FEATURE [Sketcher::SketchObject] Sketch001  label="sensor_wire_slot"
  FullyConstrained = true
  MapMode = 5
  Support = -> [XY_Plane001]
  expr: Constraints[11] = <<Properties>>.Sensor_Wire_Track_Width
  expr: Constraints[1] = Sketch.Constraints[1]
  sketch-geometry (7):
    g0: Circle CenterX=0 CenterY=0 CenterZ=0 NormalX=0 NormalY=0 NormalZ=1 AngleXU=0 Radius=25.7
    g1: LineSegment StartX=-4 StartY=-25.3868 StartZ=0 EndX=-4 EndY=-14.4568 EndZ=0
    g2: LineSegment StartX=-4 StartY=-14.4568 StartZ=0 EndX=4 EndY=-14.4568 EndZ=0
    g3: LineSegment StartX=4 StartY=-14.4568 StartZ=0 EndX=4 EndY=-25.3868 EndZ=0
    g4: ArcOfCircle CenterX=0 CenterY=0 CenterZ=0 NormalX=0 NormalY=0 NormalZ=1 AngleXU=0 Radius=25.7 StartAngle=4.55611 EndAngle=4.86867
    g5: GeomPoint X=0 Y=-14.4568 Z=0
    g6: Circle CenterX=0 CenterY=0 CenterZ=0 NormalX=0 NormalY=0 NormalZ=1 AngleXU=0 Radius=15
  constraints (17):
    c: Coincident(g0,g-1)
    c: Diameter(g0) = 51.4
    c: Vertical(g1)
    c: Coincident(g2,g1)
    c: Horizontal(g2)
    c: Coincident(g3,g2)
    c: Vertical(g3)
    c: Coincident(g4,g0)
    c: Coincident(g4,g1)
    c: Coincident(g4,g3)
    c: PointOnObject(g3,g0)
    c: DistanceX(g2,g2) = 8
    c: Symmetric(g2,g2,g5)
    c: PointOnObject(g5,g-2)
    c: Coincident(g6,g4)
    c: Diameter(g6) = 30
    c: PointOnObject(g2,g6)
FEATURE [PartDesign::Pocket] Pocket  label="Sensor_Wire_Slot"
  BaseFeature = -> Pad
  Direction = (0,0,-1)
  Length = 35
  Length2 = 35
  Profile = -> Sketch001
  ReferenceAxis = -> Sketch001 [N_Axis]
  Type = 4
  expr: Length = <<Properties>>.Insert_Len / 2
  expr: Length2 = <<Properties>>.Insert_Len / 2
FEATURE [Sketcher::SketchObject] Sketch002  label="handle_hole"
  FullyConstrained = true
  MapMode = 5
  Placement = pos=(0,0,0) rot=(1,0,0;1.5708rad)
  Support = -> [XZ_Plane001]
  expr: Constraints[1] = <<Properties>>.Handle_OD + <<Properties>>.Clearance * 2
  sketch-geometry (1):
    g0: Circle CenterX=0 CenterY=0 CenterZ=0 NormalX=0 NormalY=0 NormalZ=1 AngleXU=0 Radius=10.95
  constraints (2):
    c: Coincident(g0,g-1)
    c: Diameter(g0) = 21.9
FEATURE [PartDesign::Pocket] Pocket001  label="Handle_hole"
  BaseFeature = -> Pocket
  Direction = (0,1,2e-16)
  Length = 25.7
  Length2 = 25.7
  Profile = -> Sketch002
  ReferenceAxis = -> Sketch002 [N_Axis]
  Type = 4
  expr: Length = <<Properties>>.Head_ID / 2
  expr: Length2 = <<Properties>>.Head_ID / 2
FEATURE [Sketcher::SketchObject] Sketch004  label="top_sensor_hole"
  FullyConstrained = true
  MapMode = 5
  Placement = pos=(0,0,0) rot=(0.57735,0.57735,0.57735;2.0944rad)
  Support = -> [YZ_Plane001]
  expr: Constraints[20] = <<Properties>>.Head_ID
  expr: Constraints[7] = <<Properties>>.Sensor_Diameter + 4
  sketch-geometry (9):
    g0: LineSegment StartX=-25.7 StartY=-17 StartZ=0 EndX=-25.7 EndY=17 EndZ=0
    g1: LineSegment StartX=25.7 StartY=17 StartZ=0 EndX=25.7 EndY=-17 EndZ=0
    g2: LineSegment StartX=25.7 StartY=-17 StartZ=0 EndX=-25.7 EndY=-17 EndZ=0
    g3: GeomPoint X=0 Y=0 Z=0
    g4: LineSegment StartX=10.5 StartY=17 StartZ=0 EndX=25.7 EndY=17 EndZ=0
    g5: LineSegment StartX=25.7 StartY=17 StartZ=0 EndX=25.7 EndY=-17 EndZ=0
    g6: LineSegment StartX=25.7 StartY=-17 StartZ=0 EndX=10.5 EndY=-17 EndZ=0
    g7: LineSegment StartX=10.5 StartY=-17 StartZ=0 EndX=10.5 EndY=17 EndZ=0
    g8: LineSegment StartX=-25.7 StartY=17 StartZ=0 EndX=25.7 EndY=17 EndZ=0
  constraints (23):
    c: Coincident(g1,g2)
    c: Coincident(g2,g0)
    c: Horizontal(g2)
    c: Vertical(g0)
    c: Vertical(g1)
    c: Symmetric(g1,g0,g3)
    c: Coincident(g3,g-1)
    c: DistanceY(g1,g1) = 34
    c: Coincident(g4,g5)
    c: Coincident(g5,g6)
    c: Coincident(g6,g7)
    c: Horizontal(g4)
    c: Horizontal(g6)
    c: Vertical(g5)
    c: Vertical(g7)
    c: PointOnObject(g5,g2)
    c: Coincident(g7,g4)
    c: Coincident(g8,g0)
    c: Coincident(g8,g1)
    c: Horizontal(g8)
    c: DistanceX(g8,g8) = 51.4
    c: Coincident(g4,g1)
    c: DistanceX(g3,g4) = 10.5
FEATURE [PartDesign::Pocket] Pocket002  label="Top_Sensor_Hole"
  BaseFeature = -> Pocket001
  Direction = (-1,2e-16,-3e-16)
  Length = 17
  Length2 = 17
  Profile = -> Sketch004
  ReferenceAxis = -> Sketch004 [N_Axis]
  Type = 4
  expr: Length = <<Properties>>.Sensor_Diameter / 2 + 2
  expr: Length2 = <<Properties>>.Sensor_Diameter / 2 + 2
FEATURE [PartDesign::Chamfer] Chamfer
  Angle = 70
  Base = -> Pocket002 [Edge30,Edge32]
  BaseFeature = -> Pocket002
  ChamferType = 2
  FlipDirection = false
  Size = 8
  Size2 = 1
  SupportTransform = false
  UseAllEdges = false
FEATURE [Sketcher::SketchObject] Sketch003  label="spring_plate_slot"
  FullyConstrained = true
  MapMode = 5
  Support = -> [XY_Plane001]
  expr: Constraints[1] = Sketch.Constraints[1]
  expr: Constraints[3] = <<Properties>>.Sensor_Diameter + <<Properties>>.Clearance * 2
  expr: Constraints[7] = <<Properties>>.Spring_Plate_Len
  sketch-geometry (15):
    g0: Circle CenterX=0 CenterY=0 CenterZ=0 NormalX=0 NormalY=0 NormalZ=1 AngleXU=0 Radius=25.7
    g1: LineSegment StartX=-15.2 StartY=15.4669 StartZ=0 EndX=15.2 EndY=15.4669 EndZ=0
    g2: GeomPoint X=0 Y=15.4669 Z=0
    g3: LineSegment StartX=-23 StartY=11.4669 StartZ=0 EndX=23 EndY=11.4669 EndZ=0
    g4: GeomPoint X=0 Y=11.4669 Z=0
    g5: LineSegment StartX=-15.2 StartY=15.4669 StartZ=0 EndX=-21 EndY=11.4669 EndZ=0
    g6: LineSegment StartX=15.2 StartY=15.4669 StartZ=0 EndX=21 EndY=11.4669 EndZ=0
    g7: LineSegment StartX=21 StartY=11.4669 StartZ=0 EndX=23 EndY=11.4669 EndZ=0
    g8: LineSegment StartX=-21 StartY=11.4669 StartZ=0 EndX=-23 EndY=11.4669 EndZ=0
    g9: ArcOfCircle CenterX=0 CenterY=0 CenterZ=0 NormalX=0 NormalY=0 NormalZ=1 AngleXU=0 Radius=25.7 StartAngle=2.6791 EndAngle=2.80587
    g10: ArcOfCircle CenterX=0 CenterY=0 CenterZ=0 NormalX=0 NormalY=0 NormalZ=1 AngleXU=0 Radius=25.7 StartAngle=0.335723 EndAngle=0.462496
    g11: LineSegment StartX=-11 StartY=10.5 StartZ=0 EndX=-24.2652 EndY=8.46691 EndZ=0
    g12: LineSegment StartX=11 StartY=10.5 StartZ=0 EndX=24.2652 EndY=8.46691 EndZ=0
    g13: LineSegment StartX=11 StartY=10.5 StartZ=0 EndX=-11 EndY=10.5 EndZ=0
    g14: GeomPoint X=0 Y=10.5 Z=0
  constraints (39):
    c: Coincident(g0,g-1)
    c: Diameter(g0) = 51.4
    c: Horizontal(g1)
    c: DistanceX(g1,g1) = 30.4
    c: Symmetric(g1,g1,g2)
    c: PointOnObject(g2,g-2)
    c: Horizontal(g3)
    c: DistanceX(g3,g3) = 46
    c: Symmetric(g3,g3,g4)
    c: PointOnObject(g4,g-2)
    c: Coincident(g5,g1)
    c: PointOnObject(g5,g3)
    c: Coincident(g6,g1)
    c: PointOnObject(g6,g3)
    c: Coincident(g7,g6)
    c: PointOnObject(g7,g0)
    c: Horizontal(g7)
    c: Coincident(g8,g5)
    c: PointOnObject(g8,g0)
    c: Horizontal(g8)
    c: Equal(g8,g7)
    c: PointOnObject(g3,g0)
    c: DistanceY(g6,g1) = 4
    c: DistanceX(g6,g7) = 2
    c: Coincident(g9,g0)
    c: Coincident(g9,g8)
    c: Coincident(g10,g9)
    c: Coincident(g10,g7)
    c: Coincident(g13,g12)
    c: Coincident(g13,g11)
    c: Horizontal(g13)
    c: Coincident(g10,g12)
    c: Coincident(g9,g11)
    c: DistanceX(g12,g6) = 10
    c: Equal(g12,g11)
    c: DistanceY(g10,g7) = 3
    c: Symmetric(g13,g13,g14)
    c: PointOnObject(g14,g-2)
    c: DistanceY(g9,g14) = 10.5
FEATURE [PartDesign::Pocket] Pocket003  label="Spring_Plate_Slot"
  BaseFeature = -> Chamfer
  Direction = (0,0,-1)
  Length = 10
  Length2 = 10
  Profile = -> Sketch003
  ReferenceAxis = -> Sketch003 [N_Axis]
  Type = 4
FEATURE [PartDesign::Chamfer] Chamfer001
  Angle = 45
  Base = -> Pocket003 [Edge43,Edge46,Edge45,Edge47,Edge44,Edge42]
  BaseFeature = -> Pocket003
  ChamferType = 0
  FlipDirection = false
  Size = 0.5
  Size2 = 1
  SupportTransform = false
  UseAllEdges = false
FEATURE [Sketcher::SketchObject] Sketch008
  FullyConstrained = true
  MapMode = 5
  Placement = pos=(0,0,0) rot=(0.57735,0.57735,0.57735;2.0944rad)
  Support = -> [YZ_Plane001]
  expr: Constraints[16] = <<Properties>>.Sensor_Diameter + 2
  sketch-geometry (14):
    g0: LineSegment StartX=15.5 StartY=21 StartZ=0 EndX=15.5 EndY=-21 EndZ=0
    g1: LineSegment StartX=15.5 StartY=-21 StartZ=0 EndX=-19.02 EndY=-21 EndZ=0
    g2: LineSegment StartX=-19.02 StartY=-21 StartZ=0 EndX=-19.02 EndY=-16 EndZ=0
    g3: LineSegment StartX=-19.02 StartY=-16 StartZ=0 EndX=10.5 EndY=-16 EndZ=0
    g4: LineSegment StartX=10.5 StartY=-16 StartZ=0 EndX=10.5 EndY=16 EndZ=0
    g5: LineSegment StartX=10.5 StartY=16 StartZ=0 EndX=-19.02 EndY=16 EndZ=0
    g6: LineSegment StartX=-19.02 StartY=16 StartZ=0 EndX=-19.02 EndY=21 EndZ=0
    g7: LineSegment StartX=-19.02 StartY=21 StartZ=0 EndX=15.5 EndY=21 EndZ=0
    g8: GeomPoint X=10.5 Y=0 Z=0
    g9: GeomPoint X=15.5 Y=0 Z=0
    g10: GeomPoint X=15.5 Y=21 Z=0
    g11: GeomPoint X=15.5 Y=-21 Z=0
    g12: GeomPoint X=10.5 Y=16 Z=0
    g13: GeomPoint X=10.5 Y=-16 Z=0
  constraints (30):
    c: Vertical(g0)
    c: Horizontal(g1)
    c: Coincident(g2,g1)
    c: Vertical(g2)
    c: Coincident(g3,g2)
    c: Horizontal(g3)
    c: Vertical(g4)
    c: Horizontal(g5)
    c: Coincident(g6,g5)
    c: Vertical(g6)
    c: Coincident(g7,g6)
    c: Horizontal(g7)
    c: Symmetric(g10,g11,g9)
    c: Symmetric(g13,g12,g8)
    c: PointOnObject(g8,g-1)
    c: PointOnObject(g9,g-1)
    c: DistanceY(g13,g12) = 32
    c: DistanceY(g6,g6) = 5
    c: DistanceX(g8,g9) = 5
    c: DistanceX(g-1,g8) = 10.5
    c: DistanceX(g7,g10) = 34.52
    c: Coincident(g0,g10)
    c: Coincident(g7,g0)
    c: Coincident(g4,g12)
    c: Coincident(g5,g4)
    c: Coincident(g0,g11)
    c: Coincident(g4,g13)
    c: Coincident(g3,g4)
    c: Coincident(g1,g0)
    c: Equal(g3,g5)
FEATURE [PartDesign::Pocket] Pocket006
  BaseFeature = -> Chamfer001
  Direction = (-1,2e-16,-3e-16)
  Length = 4
  Length2 = 4
  Profile = -> Sketch008
  ReferenceAxis = -> Sketch008 [N_Axis]
  Type = 4
  expr: Length = <<Properties>>.Sensor_Wire_Track_Width / 2
  expr: Length2 = <<Properties>>.Sensor_Wire_Track_Width / 2
FEATURE [PartDesign::Chamfer] Chamfer003
  Angle = 65
  Base = -> Pocket006 [Edge148,Edge154]
  BaseFeature = -> Pocket006
  ChamferType = 2
  FlipDirection = false
  Size = 3
  Size2 = 1
  SupportTransform = false
  UseAllEdges = false
FEATURE [PartDesign::Chamfer] Chamfer004
  Angle = 45
  Base = -> Chamfer003 [Edge167,Edge85,Edge52,Edge56]
  BaseFeature = -> Chamfer003
  ChamferType = 0
  FlipDirection = false
  Size = 2
  Size2 = 1
  SupportTransform = false
  UseAllEdges = false
FEATURE [PartDesign::Chamfer] Chamfer005
  Angle = 45
  Base = -> Chamfer004 [Edge169,Edge38]
  BaseFeature = -> Chamfer004
  ChamferType = 1
  FlipDirection = false
  Size = 4
  Size2 = 3.999
  SupportTransform = false
  UseAllEdges = false
FEATURE [PartDesign::AdditiveCone] Cone
  Angle = 360
  AttacherType = Attacher::AttachEngine3D
  BaseFeature = -> Chamfer005
  Height = 1.5
  MapMode = 5
  Placement = pos=(0,0,35) rot=(0,0,1;0rad)
  Radius1 = 12
  Radius2 = 6
  Support = -> [Chamfer005]
FEATURE [PartDesign::AdditiveCone] Cone001
  Angle = 360
  AttacherType = Attacher::AttachEngine3D
  BaseFeature = -> Cone
  Height = 1.5
  MapMode = 5
  Placement = pos=(0,0,-35) rot=(1,0,0;3.14159rad)
  Radius1 = 12
  Radius2 = 6
  Support = -> [Cone]
FEATURE [Sketcher::SketchObject] Sketch022
  ExternalGeometry = -> [Cone001]
  FullyConstrained = true
  MapMode = 5
  Placement = pos=(2.3e-15,10.5,-35) rot=(-1,0,0;1.5708rad)
  Support = -> [Cone001]
  expr: Constraints[11] = <<Properties>>.Handle_OD + 2
  sketch-geometry (5):
    g0: LineSegment StartX=-11.75 StartY=-46.75 StartZ=0 EndX=-11.75 EndY=-23.25 EndZ=0
    g1: LineSegment StartX=-11.75 StartY=-23.25 StartZ=0 EndX=11.75 EndY=-23.25 EndZ=0
    g2: LineSegment StartX=11.75 StartY=-23.25 StartZ=0 EndX=11.75 EndY=-46.75 EndZ=0
    g3: LineSegment StartX=11.75 StartY=-46.75 StartZ=0 EndX=-11.75 EndY=-46.75 EndZ=0
    g4: GeomPoint X=-2.3e-15 Y=-35 Z=0
  constraints (12):
    c: Coincident(g0,g1)
    c: Coincident(g1,g2)
    c: Coincident(g2,g3)
    c: Coincident(g3,g0)
    c: Horizontal(g1)
    c: Horizontal(g3)
    c: Vertical(g0)
    c: Vertical(g2)
    c: Symmetric(g1,g0,g4)
    c: Coincident(g4,g-3)
    c: Equal(g2,g1)
    c: DistanceX(g1,g1) = 23.5
FEATURE [PartDesign::Pocket] Pocket010
  BaseFeature = -> Cone001
  Direction = (-2e-16,-1,2e-16)
  Length = 8
  Length2 = 5
  Placement = pos=(0,0,-35) rot=(1,0,0;3.14159rad)
  Profile = -> Sketch022
  ReferenceAxis = -> Sketch022 [N_Axis]
  Type = 0
FEATURE [Sketcher::SketchObject] Sketch024
  ExternalGeometry = -> [Cone001]
  FullyConstrained = true
  MapMode = 5
  Placement = pos=(6e-16,2.5,-35) rot=(-1,0,0;1.5708rad)
  Support = -> [Pocket010]
  expr: Constraints[11] = Sketch022.Constraints[11]
  expr: Constraints[54] = Sketch019.Constraints[43]
  expr: Constraints[55] = Sketch019.Constraints[44]
  sketch-geometry (34):
    g0: LineSegment StartX=-11.75 StartY=-46.75 StartZ=0 EndX=-11.75 EndY=-23.25 EndZ=0
    g1: LineSegment StartX=-11.75 StartY=-23.25 StartZ=0 EndX=11.75 EndY=-23.25 EndZ=0
    g2: LineSegment StartX=11.75 StartY=-23.25 StartZ=0 EndX=11.75 EndY=-46.75 EndZ=0
    g3: LineSegment StartX=11.75 StartY=-46.75 StartZ=0 EndX=-11.75 EndY=-46.75 EndZ=0
    g4: GeomPoint X=-2.4e-15 Y=-35 Z=0
    g5: LineSegment StartX=12 StartY=-37 StartZ=0 EndX=12 EndY=-33 EndZ=0
    g6: LineSegment StartX=12 StartY=-33 StartZ=0 EndX=2 EndY=-33 EndZ=0
    g7: LineSegment StartX=2 StartY=-33 StartZ=0 EndX=2 EndY=-23 EndZ=0
    g8: LineSegment StartX=2 StartY=-23 StartZ=0 EndX=-2 EndY=-23 EndZ=0
    g9: LineSegment StartX=-2 StartY=-23 StartZ=0 EndX=-2 EndY=-33 EndZ=0
    g10: LineSegment StartX=-2 StartY=-33 StartZ=0 EndX=-12 EndY=-33 EndZ=0
    g11: LineSegment StartX=-12 StartY=-33 StartZ=0 EndX=-12 EndY=-37 EndZ=0
    g12: LineSegment StartX=-12 StartY=-37 StartZ=0 EndX=-2 EndY=-37 EndZ=0
    g13: LineSegment StartX=-2 StartY=-37 StartZ=0 EndX=-2 EndY=-47 EndZ=0
    g14: LineSegment StartX=-2 StartY=-47 StartZ=0 EndX=2 EndY=-47 EndZ=0
    g15: LineSegment StartX=2 StartY=-47 StartZ=0 EndX=2 EndY=-37 EndZ=0
    g16: LineSegment StartX=2 StartY=-37 StartZ=0 EndX=12 EndY=-37 EndZ=0
    g17: LineSegment StartX=-2 StartY=-37 StartZ=0 EndX=-2 EndY=-33 EndZ=0
    g18: LineSegment StartX=-2 StartY=-33 StartZ=0 EndX=2 EndY=-33 EndZ=0
    g19: LineSegment StartX=2 StartY=-33 StartZ=0 EndX=2 EndY=-37 EndZ=0
    g20: LineSegment StartX=2 StartY=-37 StartZ=0 EndX=-2 EndY=-37 EndZ=0
    g21: GeomPoint X=0 Y=0 Z=0
    g22: LineSegment StartX=-2 StartY=-23.25 StartZ=0 EndX=2 EndY=-23.25 EndZ=0
    g23: LineSegment StartX=2 StartY=-23.25 StartZ=0 EndX=2 EndY=-33 EndZ=0
    g24: LineSegment StartX=2 StartY=-33 StartZ=0 EndX=11.75 EndY=-33 EndZ=0
    g25: LineSegment StartX=11.75 StartY=-33 StartZ=0 EndX=11.75 EndY=-37 EndZ=0
    g26: LineSegment StartX=11.75 StartY=-37 StartZ=0 EndX=2 EndY=-37 EndZ=0
    g27: LineSegment StartX=2 StartY=-37 StartZ=0 EndX=2 EndY=-46.75 EndZ=0
    g28: LineSegment StartX=2 StartY=-46.75 StartZ=0 EndX=-2 EndY=-46.75 EndZ=0
    g29: LineSegment StartX=-2 StartY=-46.75 StartZ=0 EndX=-2 EndY=-37 EndZ=0
    g30: LineSegment StartX=-2 StartY=-37 StartZ=0 EndX=-11.75 EndY=-37 EndZ=0
    g31: LineSegment StartX=-11.75 StartY=-37 StartZ=0 EndX=-11.75 EndY=-33 EndZ=0
    g32: LineSegment StartX=-11.75 StartY=-33 StartZ=0 EndX=-2 EndY=-33 EndZ=0
    g33: LineSegment StartX=-2 StartY=-33 StartZ=0 EndX=-2 EndY=-23.25 EndZ=0
  constraints (90):
    c: Coincident(g0,g1)
    c: Coincident(g1,g2)
    c: Coincident(g2,g3)
    c: Coincident(g3,g0)
    c: Horizontal(g1)
    c: Horizontal(g3)
    c: Vertical(g0)
    c: Vertical(g2)
    c: Symmetric(g1,g0,g4)
    c: Coincident(g4,g-3)
    c: Equal(g2,g1)
    c: DistanceX(g1,g1) = 23.5
    c: Vertical(g5)
    c: Coincident(g6,g5)
    c: Horizontal(g6)
    c: Coincident(g7,g6)
    c: Vertical(g7)
    c: Coincident(g8,g7)
    c: Horizontal(g8)
    c: Coincident(g9,g8)
    c: Vertical(g9)
    c: Coincident(g10,g9)
    c: Horizontal(g10)
    c: Coincident(g11,g10)
    c: Vertical(g11)
    c: Horizontal(g12)
    c: Coincident(g13,g12)
    c: Vertical(g13)
    c: Horizontal(g14)
    c: Coincident(g15,g14)
    c: Vertical(g15)
    c: Coincident(g16,g15)
    c: Coincident(g16,g5)
    c: Horizontal(g16)
    c: Equal(g5,g8)
    c: Equal(g8,g11)
    c: Equal(g11,g14)
    c: Coincident(g11,g12)
    c: Coincident(g14,g13)
    c: Equal(g16,g12)
    c: Equal(g16,g6)
    c: Equal(g7,g9)
    c: Equal(g10,g15)
    c: Coincident(g17,g18)
    c: Coincident(g18,g19)
    c: Coincident(g19,g20)
    c: Coincident(g20,g17)
    c: Horizontal(g18)
    c: Horizontal(g20)
    c: Vertical(g17)
    c: Vertical(g19)
    c: Coincident(g21,g-1)
    c: Coincident(g18,g6)
    c: Coincident(g12,g17)
    c: DistanceX(g18,g18) = 4
    c: DistanceY(g7,g7) = 10
    c: Equal(g15,g7)
    c: Symmetric(g6,g12,g4)
    c: PointOnObject(g22,g9)
    c: PointOnObject(g22,g1)
    c: Horizontal(g22)
    c: PointOnObject(g22,g7)
    c: Coincident(g23,g22)
    c: Coincident(g23,g6)
    c: Coincident(g24,g23)
    c: PointOnObject(g24,g2)
    c: Horizontal(g24)
    c: Coincident(g25,g24)
    c: PointOnObject(g25,g16)
    c: Vertical(g25)
    c: Coincident(g26,g25)
    c: Coincident(g26,g15)
    c: Coincident(g27,g26)
    c: PointOnObject(g27,g3)
    c: Vertical(g27)
    c: Coincident(g28,g27)
    c: PointOnObject(g28,g13)
    c: Horizontal(g28)
    c: Coincident(g29,g28)
    c: Coincident(g29,g12)
    c: Coincident(g30,g29)
    c: PointOnObject(g30,g0)
    c: Horizontal(g30)
    c: Coincident(g31,g30)
    c: PointOnObject(g31,g10)
    c: Vertical(g31)
    c: Coincident(g32,g31)
    c: Coincident(g32,g9)
    c: Coincident(g33,g32)
    c: Coincident(g33,g22)
FEATURE [PartDesign::Pocket] Pocket011
  BaseFeature = -> Pocket010
  Direction = (-2e-16,-1,2e-16)
  Length = 3
  Length2 = 5
  Placement = pos=(0,0,-35) rot=(1,0,0;3.14159rad)
  Profile = -> Sketch024
  ReferenceAxis = -> Sketch024 [N_Axis]
  Type = 0
FEATURE [PartDesign::Body] Body  label="HeadInstert"
  Group = -> [Sketch,Pad,Sketch001,Pocket,Sketch002,Pocket001,Sketch004,Pocket002,Chamfer,Sketch003,Pocket003,Chamfer001,Sketch008,Pocket006,Chamfer003,Chamfer004,Chamfer005,Cone,Cone001,Sketch022,Pocket010,Sketch024,Pocket011]
  Origin = -> Origin001
  Tip = -> Pocket011
PROVENANCE & LICENSES
A FreeCAD (.FCStd) document from a public repository crawl; recipes are the document's own serialized feature recipes (and, for linked parts, companion documents' recipes).
License: as declared in the source repository (recorded in the dataset sidecar).
